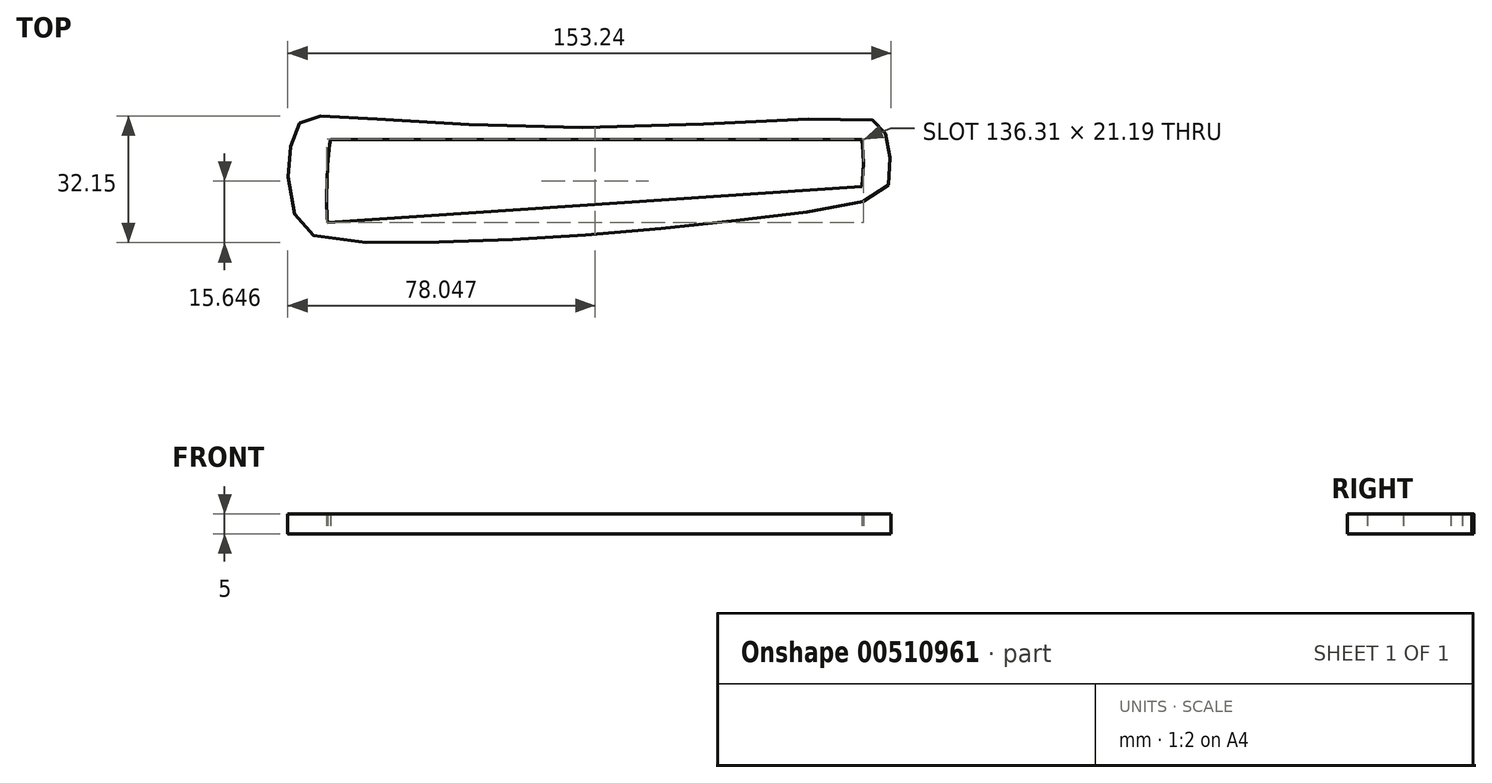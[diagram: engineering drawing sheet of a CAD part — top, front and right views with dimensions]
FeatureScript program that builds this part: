
annotation { "Feature Type Name" : "Feature", "Feature Type Description" : "" }
export const myFeature = defineFeature(function(context is Context, id is Id, definition is map)
    precondition{}
    {
        {
            var Q0;
            Q0=qCreatedBy(makeId("Top.planeOp"),FACE);
            var sketch = newSketch(context, id + "F0", { "sketchPlane" : qUnion([Q0])});
            skLineSegment(sketch, "E0", {"start": v(-68.34, 0) * mm, "end": v(66.66, 0) * mm});
            skLineSegment(sketch, "E1", {"start": v(66.66, 0) * mm, "end": v(66.66, -12) * mm, "construction": true});
            skLineSegment(sketch, "E2", {"start": v(-68.34, 0) * mm, "end": v(-69.08, -21.19) * mm, "construction": true});
            skLineSegment(sketch, "E3", {"start": v(-69.08, -21.19) * mm, "end": v(66.66, -12) * mm});
            skLineSegment(sketch, "E4", {"start": v(-71.64, 3) * mm, "end": v(69.9, 3) * mm, "construction": true});
            skLineSegment(sketch, "E5", {"start": v(69.9, 3) * mm, "end": v(69.6, -14.83) * mm, "construction": true});
            skLineSegment(sketch, "E6", {"start": v(69.6, -14.83) * mm, "end": v(-72.6, -24.45) * mm, "construction": true});
            skLineSegment(sketch, "E7", {"start": v(-72.6, -24.45) * mm, "end": v(-71.64, 3) * mm, "construction": true});
            skLineSegment(sketch, "E8", {"start": v(-71.64, 3) * mm, "end": v(-71.64, 3) * mm});
            skArc(sketch, "E9", {"start": v(66.66, -12) * mm, "mid": v(67.05, -6) * mm, "end": v(66.66, 0) * mm});
            skArc(sketch, "E10", {"start": v(-68.34, 0) * mm, "mid": v(-69.2, -10.58) * mm, "end": v(-69.08, -21.19) * mm});
            skFitSpline(sketch, "E11", {"points": [v(-79.1, -9.63) * mm, v(-78.51, -2.1) * mm, v(-76.73, 3.05) * mm, v(-74.95, 5.23) * mm, v(-68.01, 5.82) * mm, v(0, 3) * mm, v(69.7, 4.83) * mm, v(72.27, 3) * mm, v(72.86, 0) * mm, v(73.86, -5.07) * mm, v(73.66, -11.02) * mm, v(69.6, -14.83) * mm, v(43.94, -19.54) * mm, v(0, -24.1) * mm, v(-42.06, -26.08) * mm, v(-72.6, -24.45) * mm, v(-77.13, -19.93) * mm, v(-79.1, -9.63) * mm]});
            skSolve(sketch);
        }
        {
            var Q0;
            Q0 = qSketchRegion(id + "F0", true);
            extrude(context, id + "F1", {"entities" : qUnion([Q0]), "depth" : 5 * mm, "offsetDistance" : 25 * mm});
        }
    });
